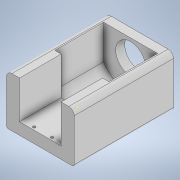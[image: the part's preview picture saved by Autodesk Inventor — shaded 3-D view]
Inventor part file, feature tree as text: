
AUTODESK INVENTOR PART (.ipt)
format: ipt  version: 2022 (Build 260153000, 153)  size: 241,152 bytes
history: native  units: mm
features: sketch x12, extrude x10, fillet x2, hole x1
ambient origin geometry x8: Origin, YZ Plane, XZ Plane, XY Plane, X Axis, Y Axis, Z Axis, Center Point
bodies: Solid1 (feature_tree)
feature tree (25):
  extrude  "Extrusion1"  Depth=75.0mm
  extrude  "Extrusion2"  Depth=8.0mm TaperAngle=0.0deg
  extrude  "Extrusion3"  Depth=42.0mm TaperAngle=0.0deg
  extrude  "Extrusion4"  Depth=36.056mm
  extrude  "Extrusion5"  Depth=30.0mm
  extrude  "Extrusion6"  Depth=18.028mm
  hole  "Hole2"  [1 undecoded]
  sketch  "Sketch9"  dims[d26=42.0mm d27=0.0mm d28=4.0mm d29=0.0mm]
  extrude  "Extrusion7"  Depth=42.0mm TaperAngle=0.0deg
  extrude  "Extrusion8"  Depth=10.0mm
  extrude  "Extrusion9"  Depth=10.0mm
  fillet  "Fillet2"  [1 undecoded]
  fillet  "Fillet3"  Radius=10.0mm
  extrude  "Extrusion10"  Depth=6.0mm
  sketch  "Sketch1"  dims[d0=75.0mm d1=91.0mm]
  sketch  "Sketch2"  dims[d2=5.0mm d3=0.0mm d10=8.0mm d11=0.0mm]
  sketch  "Sketch3"  dims[d12=15.0mm d13=0.0mm d16=42.0mm d17=0.0mm]
  sketch  "Sketch4"  dims[d18=18.028mm d19=36.056mm]
  sketch  "Sketch5"  dims[d20=30.0mm d21=30.0mm]
  sketch  "Sketch6"  dims[d22=30.0mm d23=18.028mm]
  sketch  "Sketch8"  dims[d24=18.028mm d25=35.0mm]
  sketch  "Sketch10"  dims[d43=3.0mm d44=6.0mm d45=5.0mm d46=2.0mm d47=90.0deg d48=8.0mm d49=20.594885mm d50=10.0mm]
  sketch  "Sketch11"  dims[d51=46.0mm d52=0.0mm d56=33.0mm d57=0.0mm d58=0.0mm d59=10.0mm d60=0.0mm]
  sketch  "Sketch12"  dims[d62=2.0mm d63=6.0mm]
  sketch  "Sketch13"  dims[d68=3.0mm d69=10.0mm d70=0.0mm d55=0.5mm]
note: 2 required parameter values undecoded (feature->parameter linkage not recoverable at this tier; creation-order binding heuristic only, values carry confidence <= 0.55)
